# Revit family: Legrand Plexo³ DTU
name_source: partatom
category: Equipement électrique
revit_build: Autodesk Revit 2018 (Build: 20170223_1515(x64)
units: mm (PartAtom-declared; Revit-internal decimal feet)

## family parameters
Basée sur le plan de construction = Non
Configuration du panneau = Deux colonnes, circuits au sein
Cote de connecteur circulaire = Utiliser le diamètre
Couper avec des vides une fois chargée = Non
Numéro OmniClass = 23.80.30.11.17
Partagée = Non
Point de calcul de pièce = Non
Titre OmniClass = Distribution Boards and Control Panels
Toujours verticalement = Oui
Type d'élément = Tableau de raccordement

## types (3) — shared parameters
Conditions Générale d'Utilisation = https://export.legrand.com
ETIM Class 6.0 = EC000214
Fabricant = Legrand
IK = 09
IP = 65
Image du type = <Aucun>
Matière = Polystyrène
Polystyrène
RAL = 7046
URL = www.legrand.fr
nombre arrivée force motrice = 1
norme = NF C 15-100/A2-772-3-2-4
norme ascenseur = NF P 82-210

## per-type parameters (varying)
| type | Calibre force motrice | Coffret 401995 | Coffret 401996 | Coffret 401998 | nombre départ force motrice |
| Plexo³ 12 modules 2 rangées 401995 | 32A | Oui | Non | Non |  |
| Plexo³ 12 modules 3 rangées 401998 | 80A | Non | Non | Oui | 1 |
| Plexo³ 12 modules 3 rangées 401996 | 40A | Non | Oui | Non | 1 |

note: column(s) folded — value = type name in every type: Description
